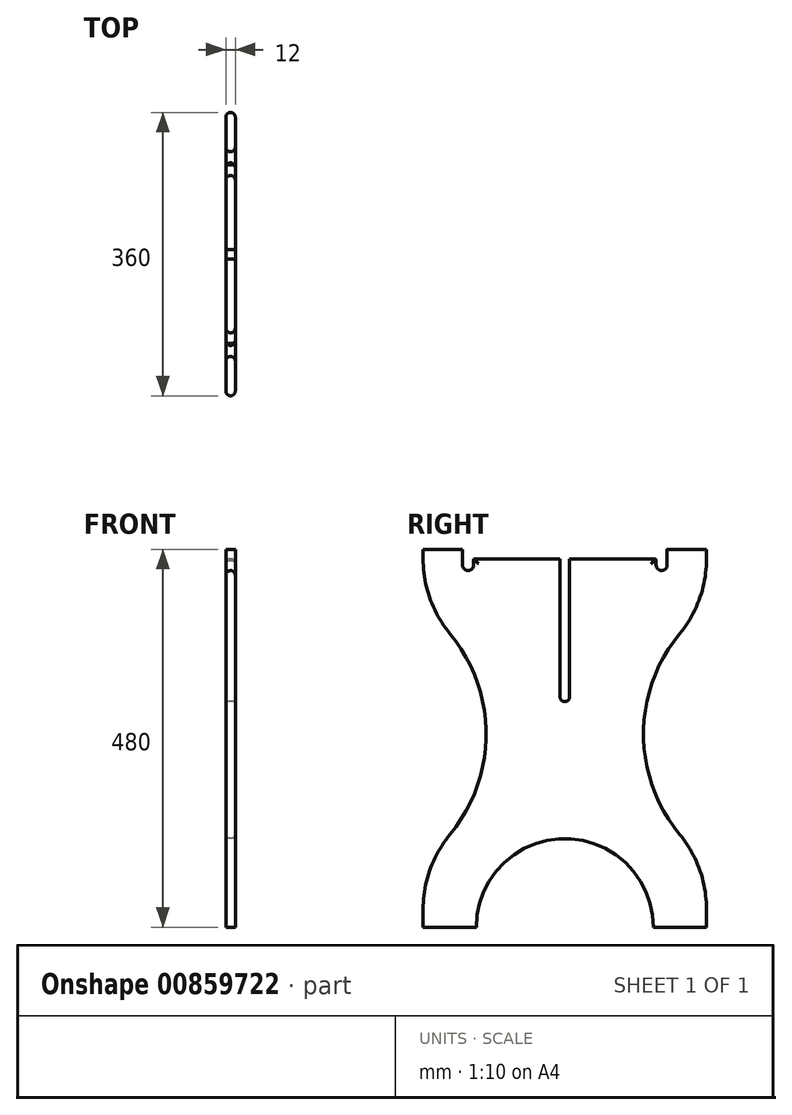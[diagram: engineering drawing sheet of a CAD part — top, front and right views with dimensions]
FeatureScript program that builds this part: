
annotation { "Feature Type Name" : "Feature", "Feature Type Description" : "" }
export const myFeature = defineFeature(function(context is Context, id is Id, definition is map)
    precondition{}
    {
        {
            var Q0;
            Q0=qCreatedBy(makeId("Right.planeOp"),FACE);
            var sketch = newSketch(context, id + "F0", { "sketchPlane" : qUnion([Q0])});
            skLineSegment(sketch, "E0.bottom", {"start": v(-180, -240) * mm, "end": v(-112.5, -240) * mm});
            skLineSegment(sketch, "E0.top", {"start": v(-180, 240) * mm, "end": v(-130, 240) * mm});
            skLineSegment(sketch, "E0.left", {"start": v(-180, -240) * mm, "end": v(-180, -217.42) * mm});
            skLineSegment(sketch, "E0.right", {"start": v(180, -240) * mm, "end": v(180, -217.42) * mm});
            skPoint(sketch, "E0.middle", {"position": v(0, 0) * mm});
            skLineSegment(sketch, "E1.0", {"start": v(-130, 228) * mm, "end": v(-130, 240) * mm});
            skLineSegment(sketch, "E2.0", {"start": v(130, 228) * mm, "end": v(130, 240) * mm});
            skLineSegment(sketch, "E3.trimOffspring", {"start": v(130, 240) * mm, "end": v(180, 240) * mm});
            skLineSegment(sketch, "E4.trimOffspring", {"start": v(112.5, -240) * mm, "end": v(180, -240) * mm});
            skArc(sketch, "E5", {"start": v(145.71, 132.55) * mm, "mid": v(100, 5.29) * mm, "end": v(145.71, -121.97) * mm});
            skArc(sketch, "E6", {"start": v(-145.71, -121.97) * mm, "mid": v(-100, 5.29) * mm, "end": v(-145.71, 132.55) * mm});
            skLineSegment(sketch, "E7.trimOffspring", {"start": v(-180, 228) * mm, "end": v(-180, 240) * mm});
            skLineSegment(sketch, "E8.trimOffspring", {"start": v(180, 228) * mm, "end": v(180, 240) * mm});
            skPoint(sketch, "E9.visualSharp", {"position": v(-180, 165.29) * mm});
            skArc(sketch, "E9.filletArc", {"start": v(-180, 228) * mm, "mid": v(-171.17, 177.3) * mm, "end": v(-145.71, 132.55) * mm});
            skPoint(sketch, "E10.visualSharp", {"position": v(-180, -154.71) * mm});
            skArc(sketch, "E10.filletArc", {"start": v(-145.71, -121.97) * mm, "mid": v(-171.17, -166.71) * mm, "end": v(-180, -217.42) * mm});
            skPoint(sketch, "E11.visualSharp", {"position": v(180, 165.29) * mm});
            skArc(sketch, "E11.filletArc", {"start": v(145.71, 132.55) * mm, "mid": v(171.17, 177.3) * mm, "end": v(180, 228) * mm});
            skPoint(sketch, "E12.visualSharp", {"position": v(180, -154.71) * mm});
            skArc(sketch, "E12.filletArc", {"start": v(180, -217.42) * mm, "mid": v(171.17, -166.71) * mm, "end": v(145.71, -121.97) * mm});
            skArc(sketch, "E13", {"start": v(116, 220) * mm, "mid": v(123, 213) * mm, "end": v(130, 220) * mm});
            skArc(sketch, "E14", {"start": v(-130, 220) * mm, "mid": v(-123, 213) * mm, "end": v(-116, 220) * mm});
            skLineSegment(sketch, "E15", {"start": v(-130, 228) * mm, "end": v(-130, 220) * mm});
            skLineSegment(sketch, "E16", {"start": v(-116, 220) * mm, "end": v(-116, 226) * mm});
            skLineSegment(sketch, "E17.trimOffspring", {"start": v(-114, 228) * mm, "end": v(-6, 228) * mm});
            skLineSegment(sketch, "E18", {"start": v(130, 228) * mm, "end": v(130, 220) * mm});
            skLineSegment(sketch, "E19", {"start": v(116, 220) * mm, "end": v(116, 226) * mm});
            skPoint(sketch, "E20.visualSharp", {"position": v(-115.99, 228) * mm});
            skArc(sketch, "E20.filletArc", {"start": v(-114, 228) * mm, "mid": v(-115.4, 227.42) * mm, "end": v(-116, 226) * mm});
            skPoint(sketch, "E21.visualSharp", {"position": v(116, 228) * mm});
            skArc(sketch, "E21.filletArc", {"start": v(116, 226) * mm, "mid": v(115.41, 227.41) * mm, "end": v(114, 228) * mm});
            skArc(sketch, "E22.MirrorCS", {"start": v(6, 52.5) * mm, "mid": v(0, 46.5) * mm, "end": v(-6, 52.5) * mm});
            skLineSegment(sketch, "E23.MirrorCS", {"start": v(-6, 228) * mm, "end": v(-6, 52.5) * mm});
            skLineSegment(sketch, "E24.MirrorCS", {"start": v(6, 228) * mm, "end": v(6, 52.5) * mm});
            skArc(sketch, "E25", {"start": v(112.5, -240) * mm, "mid": v(0, -127.5) * mm, "end": v(-112.5, -240) * mm});
            skLineSegment(sketch, "E26.trimOffspring", {"start": v(6, 228) * mm, "end": v(114, 228) * mm});
            skPoint(sketch, "E27.MirrorCS.end.orphan", {"position": v(6, 52.5) * mm});
            skSolve(sketch);
        }
        {
            var Q0;
            Q0=makeQuery(id+"F0.imprint","IMPRINT",FACE,{"disambiguationData":[TD([[makeQuery(id+"F0.imprint","IMPRINT",EDGE,{"derivedFrom":sQuery(id+"F0.wireOp",EDGE,"E0.bottom")}),1.0]])]});
            extrude(context, id + "F1", {"entities" : qUnion([Q0]), "depth" : 12 * mm, "offsetDistance" : 25 * mm});
        }
        {
            var Q0;
            Q0=makeQuery(id+"F1.opExtrude","CAP_EDGE",EDGE,{"disambiguationData":[OSD([sQuery(id+"F0.wireOp",EDGE,"E9.filletArc")])],"isStart":true});
            var Q1;
            Q1=makeQuery(id+"F1.opExtrude","CAP_EDGE",EDGE,{"disambiguationData":[OSD([sQuery(id+"F0.wireOp",EDGE,"E0.left")])],"isStart":false});
            var Q2;
            Q2=makeQuery(id+"F1.opExtrude","CAP_EDGE",EDGE,{"disambiguationData":[OSD([sQuery(id+"F0.wireOp",EDGE,"E12.filletArc")])],"isStart":true});
            var Q3;
            Q3=makeQuery(id+"F1.opExtrude","CAP_EDGE",EDGE,{"disambiguationData":[OSD([sQuery(id+"F0.wireOp",EDGE,"E5")])],"isStart":false});
            var Q4;
            Q4=makeQuery(id+"F1.opExtrude","CAP_EDGE",EDGE,{"disambiguationData":[OSD([sQuery(id+"F0.wireOp",EDGE,"E25")])],"isStart":false});
            var Q5;
            Q5=makeQuery(id+"F1.opExtrude","CAP_EDGE",EDGE,{"disambiguationData":[OSD([sQuery(id+"F0.wireOp",EDGE,"E25")])],"isStart":true});
            var Q6;
            Q6=makeQuery(id+"F1.opExtrude","CAP_EDGE",EDGE,{"disambiguationData":[OSD([sQuery(id+"F0.wireOp",EDGE,"E2.0"),sQuery(id+"F0.wireOp",EDGE,"E18")])],"isStart":false});
            var Q7;
            Q7=makeQuery(id+"F1.opExtrude","CAP_EDGE",EDGE,{"disambiguationData":[OSD([sQuery(id+"F0.wireOp",EDGE,"E1.0"),sQuery(id+"F0.wireOp",EDGE,"E15")])],"isStart":true});
            var Q8;
            Q8=makeQuery(id+"F1.opExtrude","CAP_EDGE",EDGE,{"disambiguationData":[OSD([sQuery(id+"F0.wireOp",EDGE,"E2.0"),sQuery(id+"F0.wireOp",EDGE,"E18")])],"isStart":true});
            var Q9;
            Q9=makeQuery(id+"F1.opExtrude","CAP_EDGE",EDGE,{"disambiguationData":[OSD([sQuery(id+"F0.wireOp",EDGE,"E1.0"),sQuery(id+"F0.wireOp",EDGE,"E15")])],"isStart":false});
            fillet(context, id + "F2", {"entities" : qUnion([Q0, Q1, Q2, Q3, Q4, Q5, Q6, Q7, Q8, Q9]), "radius" : 6 * mm, "tangentPropagation" : true, "allowEdgeOverflow" : false});
        }
    });
